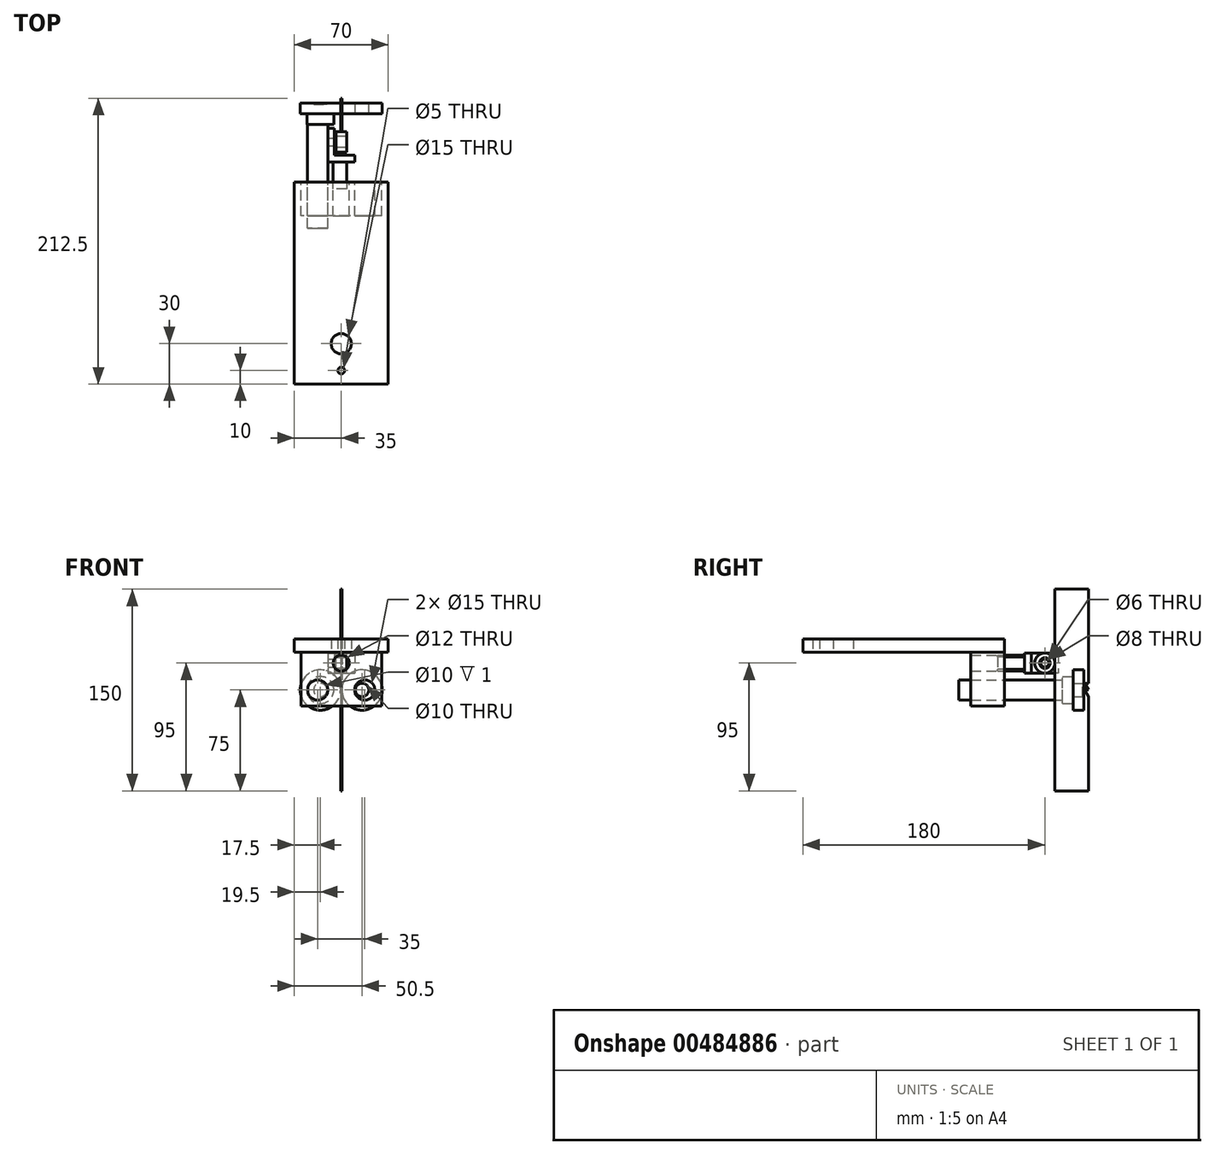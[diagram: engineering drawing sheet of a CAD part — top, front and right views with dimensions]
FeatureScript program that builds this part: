
annotation { "Feature Type Name" : "Feature", "Feature Type Description" : "" }
export const myFeature = defineFeature(function(context is Context, id is Id, definition is map)
    precondition{}
    {
        {
            var Q0;
            Q0=qCreatedBy(makeId("Front.planeOp"),FACE);
            var sketch = newSketch(context, id + "F0", { "sketchPlane" : qUnion([Q0])});
            skLineSegment(sketch, "E0.bottom", {"start": v(0.5, 75) * mm, "end": v(-0.5, 75) * mm});
            skLineSegment(sketch, "E0.top", {"start": v(0.5, -75) * mm, "end": v(-0.5, -75) * mm});
            skLineSegment(sketch, "E0.left", {"start": v(0.5, 75) * mm, "end": v(0.5, -75) * mm});
            skLineSegment(sketch, "E0.right", {"start": v(-0.5, 75) * mm, "end": v(-0.5, -75) * mm});
            skPoint(sketch, "E0.middle", {"position": v(0, 0) * mm});
            skSolve(sketch);
        }
        {
            var Q0;
            Q0=makeQuery(id+"F0.imprint","IMPRINT",FACE,{"disambiguationData":[TD([[makeQuery(id+"F0.imprint","IMPRINT",EDGE,{"derivedFrom":sQuery(id+"F0.wireOp",EDGE,"E0.bottom")}),1.0]])]});
            extrude(context, id + "F1", {"entities" : qUnion([Q0]), "endBound" : BoundingType.SYMMETRIC, "depth" : 25 * mm});
        }
        {
            var Q0;
            Q0=makeQuery(id+"F1.opExtrude","SWEPT_FACE",FACE,{"disambiguationData":[OSD([sQuery(id+"F0.wireOp",EDGE,"E0.right")])]});
            var sketch = newSketch(context, id + "F2", { "sketchPlane" : qUnion([Q0])});
            skLineSegment(sketch, "E1.0", {"start": v(-12.5, 5) * mm, "end": v(-12.5, -5) * mm});
            skLineSegment(sketch, "E2", {"start": v(0, 0) * mm, "end": v(-38.27, 0) * mm, "construction": true});
            skLineSegment(sketch, "E3", {"start": v(-12.5, 0) * mm, "end": v(-9.5, 5) * mm});
            skLineSegment(sketch, "E4", {"start": v(-9.5, 5) * mm, "end": v(-12.5, 5) * mm});
            skLineSegment(sketch, "E5", {"start": v(-12.5, 0) * mm, "end": v(-9.5, 0) * mm});
            skLineSegment(sketch, "E6", {"start": v(-9.5, 0) * mm, "end": v(-12.5, -5) * mm});
            skPoint(sketch, "E7.orphan", {"position": v(-12.5, 75) * mm});
            skPoint(sketch, "E8.orphan", {"position": v(-12.5, -75) * mm});
            skSolve(sketch);
        }
        {
            var Q0;
            {var subQ2=sQuery(id+"F2.wireOp",EDGE,"E3");Q0=makeQuery(id+"F2.imprint","IMPRINT",FACE,{"disambiguationData":[TD([[makeQuery(id+"F2.imprint","IMPRINT",EDGE,{"derivedFrom":subQ2}),1.0]])]});}
            var Q1;
            {var subQ2=sQuery(id+"F2.wireOp",EDGE,"E5");Q1=makeQuery(id+"F2.imprint","IMPRINT",FACE,{"disambiguationData":[TD([[makeQuery(id+"F2.imprint","IMPRINT",EDGE,{"derivedFrom":subQ2}),-1.0]])]});}
            extrude(context, id + "F3", {"entities" : qUnion([Q0, Q1]), "operationType" : NewBodyOperationType.REMOVE, "endBound" : BoundingType.THROUGH_ALL, "oppositeDirection" : true, "depth" : 25 * mm});
        }
        {
            var Q0;
            Q0=qCreatedBy(makeId("Front.planeOp"),FACE);
            cPlane(context, id + "F4", {"entities" : qUnion([Q0]), "cplaneType" : CPlaneType.OFFSET, "offset" : 5 * mm, "oppositeDirection" : true, "width" : 150 * mm, "height" : 150 * mm});
        }
        {
            var Q0;
            Q0=qCreatedBy(id+"F4.planeOp",FACE);
            var sketch = newSketch(context, id + "F5", { "sketchPlane" : qUnion([Q0])});
            skLineSegment(sketch, "E9", {"start": v(0, 0) * mm, "end": v(15.5, 0) * mm, "construction": true});
            skCircle(sketch, "E10", {"center": v(15.5, 0) * mm, "radius": 15 * mm});
            skCircle(sketch, "E11", {"center": v(15.5, 0) * mm, "radius": 5 * mm});
            skSolve(sketch);
        }
        {
            var Q0;
            Q0=makeQuery(id+"F5.imprint","IMPRINT",FACE,{"disambiguationData":[TD([[makeQuery(id+"F5.imprint","IMPRINT",EDGE,{"derivedFrom":sQuery(id+"F5.wireOp",EDGE,"E10")}),1.0]])]});
            extrude(context, id + "F6", {"entities" : qUnion([Q0]), "operationType" : NewBodyOperationType.ADD, "endBound" : BoundingType.SYMMETRIC, "depth" : 8 * mm});
        }
        {
            var Q0;
            Q0=qCreatedBy(makeId("Right.planeOp"),FACE);
            var sketch = newSketch(context, id + "F7", { "sketchPlane" : qUnion([Q0])});
            skLineSegment(sketch, "E12", {"start": v(0, 20) * mm, "end": v(-20, 20) * mm, "construction": true});
            skCircle(sketch, "E13", {"center": v(-20, 20) * mm, "radius": 7.5 * mm});
            skCircle(sketch, "E14", {"center": v(-20, 20) * mm, "radius": 4 * mm});
            skLineSegment(sketch, "E15", {"start": v(0, 0) * mm, "end": v(0, 20) * mm, "construction": true});
            skSolve(sketch);
        }
        {
            var Q0;
            Q0=makeQuery(id+"F7.imprint","IMPRINT",FACE,{"disambiguationData":[TD([[makeQuery(id+"F7.imprint","IMPRINT",EDGE,{"derivedFrom":sQuery(id+"F7.wireOp",EDGE,"E13")}),1.0]])]});
            extrude(context, id + "F8", {"entities" : qUnion([Q0]), "endBound" : BoundingType.SYMMETRIC, "depth" : 8 * mm});
        }
        {
            var Q0;
            Q0=makeQuery(id+"F6.opExtrude","SWEPT_BODY",BODY,{"disambiguationData":[OSD([sQuery(id+"F5.wireOp",EDGE,"E10"),sQuery(id+"F5.wireOp",EDGE,"E11")])]});
            var Q1;
            Q1=qCreatedBy(makeId("Right.planeOp"),FACE);
            mirror(context, id + "F9", {"operationType" : NewBodyOperationType.ADD, "entities" : qUnion([Q0]), "mirrorPlane" : qUnion([Q1])});
        }
        {
            var Q0;
            Q0=makeQuery(id+"F9.opPattern","COPY",FACE,{"derivedFrom":makeQuery(id+"F6.opExtrude","CAP_FACE",FACE,{"disambiguationData":[OSD([sQuery(id+"F5.wireOp",EDGE,"E10"),sQuery(id+"F5.wireOp",EDGE,"E11")])],"isStart":false}),"instanceName":"1"});
            var sketch = newSketch(context, id + "F10", { "sketchPlane" : qUnion([Q0])});
            skCircle(sketch, "E16.0", {"center": v(-15.5, 0) * mm, "radius": 5 * mm});
            skCircle(sketch, "E17", {"center": v(-15.5, 0) * mm, "radius": 10 * mm});
            skLineSegment(sketch, "E18", {"start": v(-15.5, 0) * mm, "end": v(-25.5, 0) * mm, "construction": true});
            skCircle(sketch, "E19", {"center": v(-17.5, 0) * mm, "radius": 7.5 * mm});
            skSolve(sketch);
        }
        {
            var Q0;
            Q0 = qSketchRegion(id + "F10", true);
            var Q1;
            Q1=makeQuery(id+"F10.imprint","IMPRINT",FACE,{"disambiguationData":[TD([[makeQuery(id+"F10.imprint","IMPRINT",EDGE,{"derivedFrom":sQuery(id+"F10.wireOp",EDGE,"E16.0")}),-1.0]])]});
            var Q2;
            Q2=makeQuery(id+"F10.imprint","IMPRINT",FACE,{"disambiguationData":[TD([[makeQuery(id+"F10.imprint","IMPRINT",EDGE,{"derivedFrom":sQuery(id+"F10.wireOp",EDGE,"E16.0")}),1.0]])]});
            extrude(context, id + "F11", {"entities" : qUnion([Q0, Q1, Q2]), "depth" : 8 * mm});
        }
        {
            var Q0;
            Q0=makeQuery(id+"F10.imprint","IMPRINT",FACE,{"disambiguationData":[TD([[makeQuery(id+"F10.imprint","IMPRINT",EDGE,{"derivedFrom":sQuery(id+"F10.wireOp",EDGE,"E16.0")}),-1.0]])]});
            extrude(context, id + "F12", {"entities" : qUnion([Q0]), "operationType" : NewBodyOperationType.ADD, "oppositeDirection" : true, "depth" : 7 * mm});
        }
        {
            var Q0;
            Q0=makeQuery(id+"F10.imprint","IMPRINT",FACE,{"disambiguationData":[TD([[makeQuery(id+"F10.imprint","IMPRINT",EDGE,{"derivedFrom":sQuery(id+"F10.wireOp",EDGE,"E16.0")}),1.0]])]});
            extrude(context, id + "F13", {"entities" : qUnion([Q0]), "operationType" : NewBodyOperationType.ADD, "depth" : 85 * mm});
        }
        {
            var Q0;
            Q0=makeQuery(id+"F13.boolean.opBoolean","SPLIT",FACE,{"disambiguationData":[TD([makeQuery(id+"F13.opExtrude","SWEPT_FACE",FACE,{"disambiguationData":[OSD([sQuery(id+"F10.wireOp",EDGE,"E16.0")])]})])],"derivedFrom":makeQuery(id+"F11.opExtrude","CAP_FACE",FACE,{"disambiguationData":[OSD([sQuery(id+"F10.wireOp",EDGE,"E17")])],"isStart":false})});
            var Q1;
            Q1=makeQuery(id+"F13.opExtrude","CAP_FACE",FACE,{"disambiguationData":[OSD([sQuery(id+"F10.wireOp",EDGE,"E16.0"),sQuery(id+"F10.wireOp",EDGE,"E19")])],"isStart":false});
            extrude(context, id + "F14", {"entities" : qUnion([Q0]), "operationType" : NewBodyOperationType.ADD, "endBound" : BoundingType.UP_TO_SURFACE, "endBoundEntityFace" : qUnion([Q1]), "depth" : 25 * mm});
        }
        {
            var Q0;
            Q0=makeQuery(id+"F8.opExtrude","CAP_FACE",FACE,{"disambiguationData":[OSD([sQuery(id+"F7.wireOp",EDGE,"E13"),sQuery(id+"F7.wireOp",EDGE,"E14")])],"isStart":true});
            var sketch = newSketch(context, id + "F15", { "sketchPlane" : qUnion([Q0])});
            skCircle(sketch, "E20", {"center": v(20, 20) * mm, "radius": 3 * mm});
            skLineSegment(sketch, "E21.bottom", {"start": v(10, 27.5) * mm, "end": v(30, 27.5) * mm});
            skLineSegment(sketch, "E21.top", {"start": v(10, 12.5) * mm, "end": v(30, 12.5) * mm});
            skLineSegment(sketch, "E21.left", {"start": v(10, 27.5) * mm, "end": v(10, 12.5) * mm});
            skLineSegment(sketch, "E21.right", {"start": v(30, 27.5) * mm, "end": v(30, 12.5) * mm});
            skLineSegment(sketch, "E22", {"start": v(20, 20) * mm, "end": v(64.04, 20) * mm, "construction": true});
            skSolve(sketch);
        }
        {
            var Q0;
            {var subQ0=sQuery(id+"F15.wireOp",EDGE,"E21.right");Q0=makeQuery(id+"F15.imprint","IMPRINT",FACE,{"disambiguationData":[TD([[makeQuery(id+"F15.imprint","IMPRINT",EDGE,{"derivedFrom":subQ0}),-1.0]])]});}
            var Q1;
            Q1=makeQuery(id+"F15.imprint","IMPRINT",FACE,{"disambiguationData":[TD([[makeQuery(id+"F15.imprint","IMPRINT",EDGE,{"derivedFrom":makeQuery(id+"F8.opExtrude","CAP_EDGE",EDGE,{"disambiguationData":[OSD([sQuery(id+"F7.wireOp",EDGE,"E14")])],"isStart":true})}),1.0]])]});
            var Q2;
            {var subQ0=sQuery(id+"F15.wireOp",EDGE,"E21.left");Q2=makeQuery(id+"F15.imprint","IMPRINT",FACE,{"disambiguationData":[TD([[makeQuery(id+"F15.imprint","IMPRINT",EDGE,{"derivedFrom":subQ0}),1.0]])]});}
            var Q3;
            Q3=makeQuery(id+"F15.imprint","IMPRINT",FACE,{"disambiguationData":[TD([[makeQuery(id+"F15.imprint","IMPRINT",EDGE,{"derivedFrom":sQuery(id+"F15.wireOp",EDGE,"E20")}),-1.0]])]});
            extrude(context, id + "F16", {"entities" : qUnion([Q0, Q1, Q2, Q3]), "depth" : 6 * mm, "hasSecondDirection" : true, "secondDirectionOppositeDirection" : false, "secondDirectionDepth" : 1 * mm});
        }
        {
            var Q0;
            Q0=makeQuery(id+"F16.opExtrude","SWEPT_FACE",FACE,{"disambiguationData":[OSD([sQuery(id+"F15.wireOp",EDGE,"E21.right")])]});
            var sketch = newSketch(context, id + "F17", { "sketchPlane" : qUnion([Q0])});
            skLineSegment(sketch, "E23", {"start": v(0, 34.18) * mm, "end": v(0, 8.32) * mm, "construction": true});
            skLineSegment(sketch, "E24.0", {"start": v(-10, 27.5) * mm, "end": v(-10, 12.5) * mm});
            skLineSegment(sketch, "E25", {"start": v(-10, 20) * mm, "end": v(0, 20) * mm, "construction": true});
            skLineSegment(sketch, "E26.bottom", {"start": v(-10, 27.5) * mm, "end": v(10, 27.5) * mm});
            skLineSegment(sketch, "E26.top", {"start": v(-10, 12.5) * mm, "end": v(10, 12.5) * mm});
            skLineSegment(sketch, "E26.right", {"start": v(10, 27.5) * mm, "end": v(10, 12.5) * mm});
            skCircle(sketch, "E27", {"center": v(0, 20) * mm, "radius": 6 * mm});
            skSolve(sketch);
        }
        {
            var Q0;
            {var subQ2=sQuery(id+"F17.wireOp",EDGE,"E26.right");Q0=makeQuery(id+"F17.imprint","IMPRINT",FACE,{"disambiguationData":[TD([[makeQuery(id+"F17.imprint","IMPRINT",EDGE,{"derivedFrom":subQ2}),-1.0]])]});}
            var Q1;
            {var subQ2=sQuery(id+"F17.wireOp",EDGE,"E24.0");Q1=makeQuery(id+"F17.imprint","IMPRINT",FACE,{"disambiguationData":[TD([[makeQuery(id+"F17.imprint","IMPRINT",EDGE,{"derivedFrom":subQ2}),1.0]])]});}
            extrude(context, id + "F18", {"entities" : qUnion([Q0, Q1]), "operationType" : NewBodyOperationType.ADD, "depth" : 5 * mm});
        }
        {
            var Q0;
            {var subQ0=sQuery(id+"F17.wireOp",EDGE,"E27");var subQ1=makeQuery(id+"F16.opExtrude","CAP_EDGE",EDGE,{"disambiguationData":[OSD([sQuery(id+"F15.wireOp",EDGE,"E21.right")])],"isStart":true});var subQ2=makeQuery(id+"F17.imprint","INTERSECT",VERTEX,{"disambiguationData":[OD(0.0)],"derivedFrom":[subQ1,subQ0]});Q0=makeQuery(id+"F17.imprint","IMPRINT",FACE,{"disambiguationData":[TD([[makeQuery(id+"F17.imprint","IMPRINT",EDGE,{"disambiguationData":[TD([[subQ2,1.0]])],"derivedFrom":subQ0}),1.0]])]});}
            var Q1;
            {var subQ0=sQuery(id+"F17.wireOp",EDGE,"E27");var subQ1=makeQuery(id+"F16.opExtrude","CAP_EDGE",EDGE,{"disambiguationData":[OSD([sQuery(id+"F15.wireOp",EDGE,"E21.right")])],"isStart":true});var subQ2=makeQuery(id+"F17.imprint","INTERSECT",VERTEX,{"disambiguationData":[OD(0.0)],"derivedFrom":[subQ1,subQ0]});Q1=makeQuery(id+"F17.imprint","IMPRINT",FACE,{"disambiguationData":[TD([[makeQuery(id+"F17.imprint","IMPRINT",EDGE,{"disambiguationData":[TD([[subQ2,-1.0]])],"derivedFrom":subQ0}),1.0]])]});}
            extrude(context, id + "F19", {"entities" : qUnion([Q0, Q1]), "operationType" : NewBodyOperationType.ADD, "depth" : 25 * mm});
        }
        {
            var Q0;
            Q0=makeQuery(id+"F19.opExtrude","CAP_FACE",FACE,{"disambiguationData":[OSD([sQuery(id+"F17.wireOp",EDGE,"E27")])],"isStart":false});
            var sketch = newSketch(context, id + "F20", { "sketchPlane" : qUnion([Q0])});
            skArc(sketch, "E28.0", {"start": v(4, 15.53) * mm, "mid": v(6, 20) * mm, "end": v(4, 24.47) * mm});
            skLineSegment(sketch, "E29", {"start": v(0, 20) * mm, "end": v(4, 20) * mm, "construction": true});
            skLineSegment(sketch, "E30", {"start": v(4, 24.47) * mm, "end": v(4, 15.53) * mm});
            skLineSegment(sketch, "E31", {"start": v(4, 20) * mm, "end": v(6, 20) * mm, "construction": true});
            skSolve(sketch);
        }
        {
            var Q0;
            Q0=makeQuery(id+"F20.imprint","IMPRINT",FACE,{"disambiguationData":[TD([[makeQuery(id+"F20.imprint","IMPRINT",EDGE,{"derivedFrom":sQuery(id+"F20.wireOp",EDGE,"E28.0")}),1.0]])]});
            var Q1;
            Q1=makeQuery(id+"F18.opExtrude","CAP_FACE",FACE,{"disambiguationData":[OSD([sQuery(id+"F17.wireOp",EDGE,"E26.bottom"),sQuery(id+"F17.wireOp",EDGE,"E26.top"),sQuery(id+"F17.wireOp",EDGE,"E24.0"),sQuery(id+"F17.wireOp",EDGE,"E26.right"),sQuery(id+"F17.wireOp",EDGE,"E27")])],"isStart":false});
            extrude(context, id + "F21", {"entities" : qUnion([Q0]), "operationType" : NewBodyOperationType.REMOVE, "endBound" : BoundingType.UP_TO_SURFACE, "oppositeDirection" : true, "endBoundEntityFace" : qUnion([Q1]), "depth" : 25 * mm});
        }
        {
            var Q0;
            Q0=qCreatedBy(makeId("Front.planeOp"),FACE);
            cPlane(context, id + "F22", {"entities" : qUnion([Q0]), "cplaneType" : CPlaneType.OFFSET, "offset" : 50 * mm, "width" : 150 * mm, "height" : 150 * mm});
        }
        {
            var Q0;
            Q0=qCreatedBy(id+"F22.planeOp",FACE);
            var sketch = newSketch(context, id + "F23", { "sketchPlane" : qUnion([Q0])});
            skArc(sketch, "E32.0", {"start": v(4, 24.47) * mm, "mid": v(-6, 20) * mm, "end": v(4, 15.53) * mm, "construction": true});
            skCircle(sketch, "E33.0", {"center": v(-17.5, 0) * mm, "radius": 7.5 * mm});
            skLineSegment(sketch, "E34", {"start": v(0, 33.4) * mm, "end": v(0, -70.07) * mm, "construction": true});
            skLineSegment(sketch, "E35", {"start": v(-17.5, 0) * mm, "end": v(0, 0) * mm, "construction": true});
            skPoint(sketch, "E36.middle", {"position": v(0, 0) * mm});
            skCircle(sketch, "E37", {"center": v(0, 20) * mm, "radius": 6 * mm});
            skCircle(sketch, "E38.MirrorC", {"center": v(17.5, 0) * mm, "radius": 7.5 * mm});
            skLineSegment(sketch, "E39.bottom", {"start": v(30, -12) * mm, "end": v(-30, -12) * mm});
            skLineSegment(sketch, "E39.top", {"start": v(30, 28) * mm, "end": v(-30, 28) * mm});
            skLineSegment(sketch, "E39.left", {"start": v(30, -12) * mm, "end": v(30, 28) * mm});
            skLineSegment(sketch, "E39.right", {"start": v(-30, -12) * mm, "end": v(-30, 28) * mm});
            skPoint(sketch, "E39.middle", {"position": v(0, 8) * mm});
            skSolve(sketch);
        }
        {
            var Q0;
            Q0=makeQuery(id+"F23.imprint","IMPRINT",FACE,{"disambiguationData":[TD([[makeQuery(id+"F23.imprint","IMPRINT",EDGE,{"derivedFrom":sQuery(id+"F23.wireOp",EDGE,"E33.0")}),-1.0]])]});
            extrude(context, id + "F24", {"entities" : qUnion([Q0]), "depth" : 25 * mm});
        }
        {
            var Q0;
            Q0=makeQuery(id+"F24.opExtrude","SWEPT_FACE",FACE,{"disambiguationData":[OSD([sQuery(id+"F23.wireOp",EDGE,"E39.top")])]});
            var sketch = newSketch(context, id + "F25", { "sketchPlane" : qUnion([Q0])});
            skLineSegment(sketch, "E40", {"start": v(0, -70.36) * mm, "end": v(0, -173.82) * mm, "construction": true});
            skLineSegment(sketch, "E41.bottom", {"start": v(35, -200) * mm, "end": v(-35, -200) * mm});
            skLineSegment(sketch, "E41.top", {"start": v(35, -50) * mm, "end": v(-35, -50) * mm});
            skLineSegment(sketch, "E41.left", {"start": v(35, -200) * mm, "end": v(35, -50) * mm});
            skLineSegment(sketch, "E41.right", {"start": v(-35, -200) * mm, "end": v(-35, -50) * mm});
            skPoint(sketch, "E41.middle", {"position": v(0, -125) * mm});
            skCircle(sketch, "E42", {"center": v(0, -170) * mm, "radius": 7.5 * mm});
            skLineSegment(sketch, "E43", {"start": v(0, -200) * mm, "end": v(0, -190) * mm, "construction": true});
            skPoint(sketch, "E43.endSnap0", {"position": v(0, -200) * mm});
            skCircle(sketch, "E44", {"center": v(0, -190) * mm, "radius": 2.5 * mm});
            skSolve(sketch);
        }
        {
            var Q0;
            Q0=makeQuery(id+"F25.imprint","IMPRINT",FACE,{"disambiguationData":[TD([[makeQuery(id+"F25.imprint","IMPRINT",EDGE,{"derivedFrom":sQuery(id+"F25.wireOp",EDGE,"E41.bottom")}),-1.0]])]});
            var Q1;
            {var subQ1=sQuery(id+"F23.wireOp",EDGE,"E39.top");Q1=makeQuery(id+"F25.imprint","IMPRINT",FACE,{"disambiguationData":[TD([[makeQuery(id+"F25.imprint","IMPRINT",EDGE,{"derivedFrom":makeQuery(id+"F24.opExtrude","CAP_EDGE",EDGE,{"disambiguationData":[OSD([subQ1])],"isStart":false})}),-1.0]])]});}
            extrude(context, id + "F26", {"entities" : qUnion([Q0, Q1]), "depth" : 10 * mm});
        }
    });
